# Revit family: PV
name_source: partatom
category: Lighting Fixtures
revit_build: Autodesk Revit MEP 2012 (Build: 20110309_2315(x64)
units: mm (PartAtom-declared; Revit-internal decimal feet)

## types (13) — shared parameters
Apparent Load = 0 VA
Default Elevation = 48 "
Description = The Pivot® uses energy efficient fluorescent lamps and electronic ballasts in a small compact luminaire design
Glass = Hubbell-Glass-Frosted
Lamp = LED
Load Classification = Lighting
Manufacturer = Architectural Area Lighting
Manufacturer Fax = (626)-369-2695
Model = PV
Product Documentation Link = http://cdn.aal.net
Product Page URL = http://www.aal.net
URL = http://www.aal.net
Voltage = 120 V
Wattage Comments = 14-55W

## per-type parameters (varying)
| type | Backbox |
| PV - ATG | Hubbell-Aluminum-Antique Green |
| PV - AWT | Hubbell-Aluminum-Artic White |
| PV - BLK | Hubbell-Aluminum-Black |
| PV - BRM | Hubbell-Aluminum-Metalic Bronze |
| PV - CRT | Hubbell-Aluminum-Corten |
| PV - DBZ | Hubbell-Aluminum-Dark Bronze |
| PV - DGN | Hubbell-Aluminum-Dark Green |
| PV - LGY | Hubbell-Aluminum-Light Grey |
| PV - MAL | Hubbell-Aluminum-Matte |
| PV - MDG | Hubbell-Aluminum-Medium Grey |
| PV - MTB | Hubbell-Aluminum-Matte Black |
| PV - VBL | Hubbell-Aluminum-Verde Blue |
| PV - WRZ | Hubbell-Aluminum-Weathered Bronze |

## geometry (parser evidence)
native form markers: Blend x19, Sweep x12
no freeform markers — native parametric forms only
